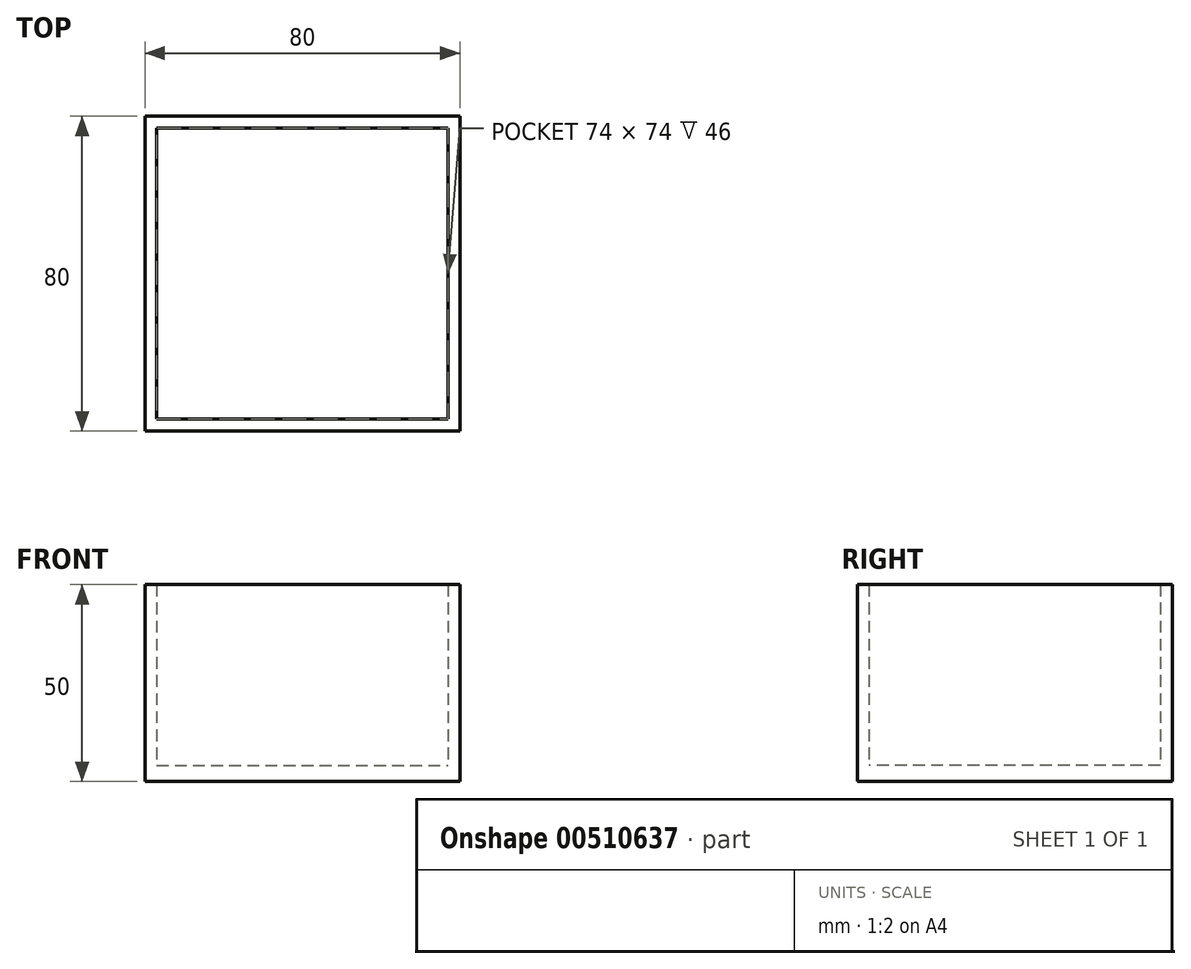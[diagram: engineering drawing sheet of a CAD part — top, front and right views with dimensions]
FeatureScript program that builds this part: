
annotation { "Feature Type Name" : "Feature", "Feature Type Description" : "" }
export const myFeature = defineFeature(function(context is Context, id is Id, definition is map)
    precondition{}
    {
        {
            var Q0;
            Q0=qCreatedBy(makeId("Top.planeOp"),FACE);
            var sketch = newSketch(context, id + "F0", { "sketchPlane" : qUnion([Q0])});
            skLineSegment(sketch, "E0.bottom", {"start": v(-40, 40) * mm, "end": v(40, 40) * mm});
            skLineSegment(sketch, "E0.top", {"start": v(-40, -40) * mm, "end": v(40, -40) * mm});
            skLineSegment(sketch, "E0.left", {"start": v(-40, 40) * mm, "end": v(-40, -40) * mm});
            skLineSegment(sketch, "E0.right", {"start": v(40, 40) * mm, "end": v(40, -40) * mm});
            skPoint(sketch, "E0.middle", {"position": v(0, 0) * mm});
            skLineSegment(sketch, "E1.bottom", {"start": v(-37, 37) * mm, "end": v(37, 37) * mm});
            skLineSegment(sketch, "E1.top", {"start": v(-37, -37) * mm, "end": v(37, -37) * mm});
            skLineSegment(sketch, "E1.left", {"start": v(-37, 37) * mm, "end": v(-37, -37) * mm});
            skLineSegment(sketch, "E1.right", {"start": v(37, 37) * mm, "end": v(37, -37) * mm});
            skSolve(sketch);
        }
        {
            var Q0;
            Q0 = qSketchRegion(id + "F0", true);
            var Q1;
            Q1=makeQuery(id+"F0.imprint","IMPRINT",FACE,{"disambiguationData":[TD([[makeQuery(id+"F0.imprint","IMPRINT",EDGE,{"derivedFrom":sQuery(id+"F0.wireOp",EDGE,"E1.bottom")}),-1.0]])]});
            extrude(context, id + "F1", {"entities" : qUnion([Q0, Q1]), "oppositeDirection" : true, "depth" : 4 * mm});
        }
        {
            var Q0;
            Q0 = qSketchRegion(id + "F0", true);
            extrude(context, id + "F2", {"entities" : qUnion([Q0]), "operationType" : NewBodyOperationType.ADD, "depth" : 46 * mm});
        }
    });
